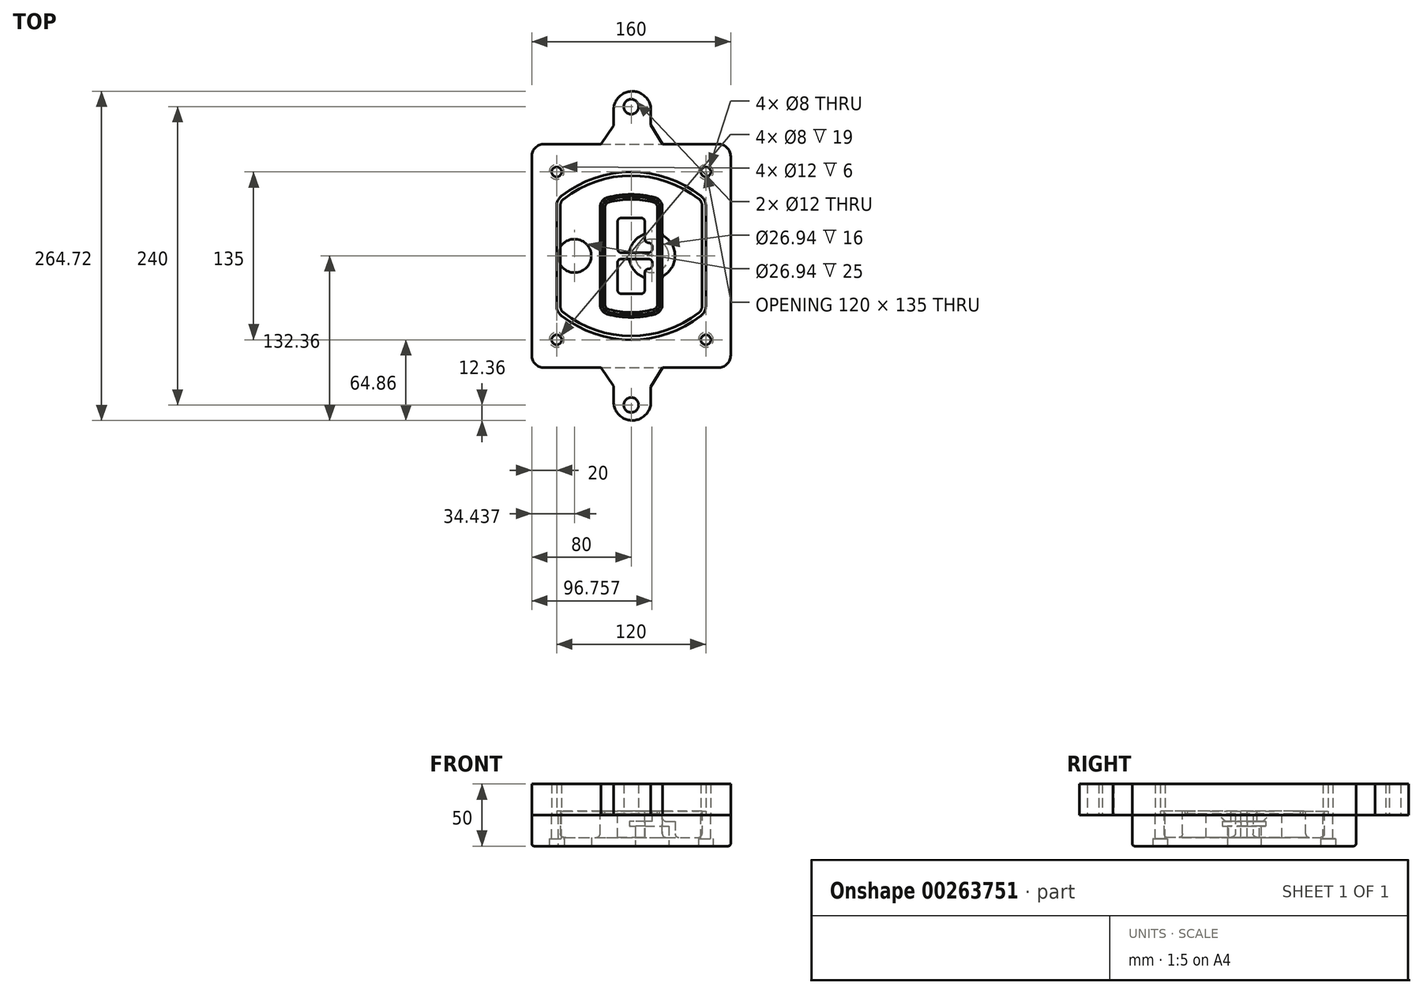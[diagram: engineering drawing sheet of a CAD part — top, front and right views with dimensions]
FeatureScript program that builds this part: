
annotation { "Feature Type Name" : "Feature", "Feature Type Description" : "" }
export const myFeature = defineFeature(function(context is Context, id is Id, definition is map)
    precondition{}
    {
        {
            var Q0;
            Q0=qCreatedBy(makeId("Top.planeOp"),FACE);
            var sketch = newSketch(context, id + "F0", { "sketchPlane" : qUnion([Q0])});
            skPoint(sketch, "E0.rect.middle", {"position": v(0, 0) * mm});
            skLineSegment(sketch, "E1.bottom", {"start": v(-70, -90) * mm, "end": v(70, -90) * mm});
            skLineSegment(sketch, "E1.top", {"start": v(-70, 90) * mm, "end": v(70, 90) * mm});
            skLineSegment(sketch, "E1.left", {"start": v(-80, -80) * mm, "end": v(-80, 80) * mm});
            skLineSegment(sketch, "E1.right", {"start": v(80, -80) * mm, "end": v(80, 80) * mm});
            skLineSegment(sketch, "E2", {"start": v(-80, 90) * mm, "end": v(80, -90) * mm, "construction": true});
            skLineSegment(sketch, "E3", {"start": v(80, 90) * mm, "end": v(-80, -90) * mm, "construction": true});
            skCircle(sketch, "E4", {"center": v(-60, 67.5) * mm, "radius": 4 * mm});
            skCircle(sketch, "E5", {"center": v(60, 67.5) * mm, "radius": 4 * mm});
            skCircle(sketch, "E6", {"center": v(60, -67.5) * mm, "radius": 4 * mm});
            skCircle(sketch, "E7", {"center": v(-60, -67.5) * mm, "radius": 4 * mm});
            skLineSegment(sketch, "E8", {"start": v(-60, 67.5) * mm, "end": v(60, 67.5) * mm, "construction": true});
            skLineSegment(sketch, "E9", {"start": v(60, 67.5) * mm, "end": v(60, -67.5) * mm, "construction": true});
            skLineSegment(sketch, "E10", {"start": v(60, -67.5) * mm, "end": v(-60, -67.5) * mm, "construction": true});
            skLineSegment(sketch, "E11", {"start": v(-60, -67.5) * mm, "end": v(-60, 67.5) * mm, "construction": true});
            skLineSegment(sketch, "E12", {"start": v(-60, 40.3) * mm, "end": v(-60, -40.3) * mm});
            skLineSegment(sketch, "E13", {"start": v(60, 40.3) * mm, "end": v(60, -40.3) * mm});
            skArc(sketch, "E14", {"start": v(56.15, 48.18) * mm, "mid": v(0, 67.5) * mm, "end": v(-56.15, 48.18) * mm});
            skArc(sketch, "E15", {"start": v(-56.15, -48.18) * mm, "mid": v(0, -67.5) * mm, "end": v(56.15, -48.18) * mm});
            skLineSegment(sketch, "E16", {"start": v(-60, 0) * mm, "end": v(60, 0) * mm, "construction": true});
            skPoint(sketch, "E17.visualSharp", {"position": v(-60, -45) * mm});
            skArc(sketch, "E17.filletArc", {"start": v(-60, -40.3) * mm, "mid": v(-58.99, -44.68) * mm, "end": v(-56.15, -48.18) * mm});
            skPoint(sketch, "E18.visualSharp", {"position": v(-60, 45) * mm});
            skArc(sketch, "E18.filletArc", {"start": v(-56.15, 48.18) * mm, "mid": v(-58.99, 44.68) * mm, "end": v(-60, 40.3) * mm});
            skPoint(sketch, "E19.visualSharp", {"position": v(60, 45) * mm});
            skArc(sketch, "E19.filletArc", {"start": v(60, 40.3) * mm, "mid": v(58.99, 44.68) * mm, "end": v(56.15, 48.18) * mm});
            skPoint(sketch, "E20.visualSharp", {"position": v(60, -45) * mm});
            skArc(sketch, "E20.filletArc", {"start": v(56.15, -48.18) * mm, "mid": v(58.99, -44.68) * mm, "end": v(60, -40.3) * mm});
            skPoint(sketch, "E21.visualSharp", {"position": v(-80, 90) * mm});
            skArc(sketch, "E21.filletArc", {"start": v(-70, 90) * mm, "mid": v(-77.07, 87.07) * mm, "end": v(-80, 80) * mm});
            skPoint(sketch, "E22.visualSharp", {"position": v(80, 90) * mm});
            skArc(sketch, "E22.filletArc", {"start": v(80, 80) * mm, "mid": v(77.07, 87.07) * mm, "end": v(70, 90) * mm});
            skPoint(sketch, "E23.visualSharp", {"position": v(80, -90) * mm});
            skArc(sketch, "E23.filletArc", {"start": v(70, -90) * mm, "mid": v(77.07, -87.07) * mm, "end": v(80, -80) * mm});
            skPoint(sketch, "E24.visualSharp", {"position": v(-80, -90) * mm});
            skArc(sketch, "E24.filletArc", {"start": v(-80, -80) * mm, "mid": v(-77.07, -87.07) * mm, "end": v(-70, -90) * mm});
            skArc(sketch, "E25.0", {"start": v(57, 40.3) * mm, "mid": v(56.3, 43.36) * mm, "end": v(54.3, 45.81) * mm});
            skLineSegment(sketch, "E25.1", {"start": v(57, 40.3) * mm, "end": v(57, -40.3) * mm});
            skArc(sketch, "E25.2", {"start": v(54.3, -45.81) * mm, "mid": v(56.3, -43.36) * mm, "end": v(57, -40.3) * mm});
            skArc(sketch, "E25.3", {"start": v(-54.3, -45.81) * mm, "mid": v(0, -64.5) * mm, "end": v(54.3, -45.81) * mm});
            skArc(sketch, "E25.4", {"start": v(-57, -40.3) * mm, "mid": v(-56.3, -43.36) * mm, "end": v(-54.3, -45.81) * mm});
            skArc(sketch, "E25.5", {"start": v(54.3, 45.81) * mm, "mid": v(0, 64.5) * mm, "end": v(-54.3, 45.81) * mm});
            skLineSegment(sketch, "E25.6", {"start": v(-57, 40.3) * mm, "end": v(-57, -40.3) * mm});
            skArc(sketch, "E25.7", {"start": v(-54.3, 45.81) * mm, "mid": v(-56.3, 43.36) * mm, "end": v(-57, 40.3) * mm});
            skArc(sketch, "E26.0", {"start": v(-58.62, 51.33) * mm, "mid": v(-62.58, 46.43) * mm, "end": v(-64, 40.3) * mm});
            skArc(sketch, "E26.1", {"start": v(58.62, 51.33) * mm, "mid": v(0, 71.5) * mm, "end": v(-58.62, 51.33) * mm});
            skArc(sketch, "E26.2", {"start": v(64, 40.3) * mm, "mid": v(62.58, 46.43) * mm, "end": v(58.62, 51.33) * mm});
            skLineSegment(sketch, "E26.3", {"start": v(64, 40.3) * mm, "end": v(64, -40.3) * mm});
            skArc(sketch, "E26.4", {"start": v(58.62, -51.33) * mm, "mid": v(62.58, -46.43) * mm, "end": v(64, -40.3) * mm});
            skLineSegment(sketch, "E26.5", {"start": v(-64, 40.3) * mm, "end": v(-64, -40.3) * mm});
            skArc(sketch, "E26.6", {"start": v(-58.62, -51.33) * mm, "mid": v(0, -71.5) * mm, "end": v(58.62, -51.33) * mm});
            skArc(sketch, "E26.7", {"start": v(-64, -40.3) * mm, "mid": v(-62.58, -46.43) * mm, "end": v(-58.62, -51.33) * mm});
            skSolve(sketch);
        }
        {
            var Q0;
            Q0=makeQuery(id+"F0.imprint","IMPRINT",FACE,{"disambiguationData":[TD([[makeQuery(id+"F0.imprint","IMPRINT",EDGE,{"derivedFrom":sQuery(id+"F0.wireOp",EDGE,"E1.bottom")}),1.0]])]});
            var Q1;
            Q1=makeQuery(id+"F0.imprint","IMPRINT",FACE,{"disambiguationData":[TD([[makeQuery(id+"F0.imprint","IMPRINT",EDGE,{"derivedFrom":sQuery(id+"F0.wireOp",EDGE,"E12")}),1.0]])]});
            var Q2;
            Q2=makeQuery(id+"F0.imprint","IMPRINT",FACE,{"disambiguationData":[TD([[makeQuery(id+"F0.imprint","IMPRINT",EDGE,{"derivedFrom":sQuery(id+"F0.wireOp",EDGE,"E25.0")}),1.0]])]});
            var Q3;
            Q3=makeQuery(id+"F0.imprint","IMPRINT",FACE,{"disambiguationData":[TD([[makeQuery(id+"F0.imprint","IMPRINT",EDGE,{"derivedFrom":sQuery(id+"F0.wireOp",EDGE,"E12")}),-1.0]])]});
            extrude(context, id + "F1", {"entities" : qUnion([Q0, Q1, Q2, Q3]), "oppositeDirection" : true, "depth" : 25 * mm});
        }
        {
            var Q0;
            Q0=makeQuery(id+"F0.imprint","IMPRINT",FACE,{"disambiguationData":[TD([[makeQuery(id+"F0.imprint","IMPRINT",EDGE,{"derivedFrom":sQuery(id+"F0.wireOp",EDGE,"E12")}),1.0]])]});
            extrude(context, id + "F2", {"entities" : qUnion([Q0]), "operationType" : NewBodyOperationType.ADD, "depth" : 3 * mm});
        }
        {
            var Q0;
            Q0=makeQuery(id+"F0.imprint","IMPRINT",FACE,{"disambiguationData":[TD([[makeQuery(id+"F0.imprint","IMPRINT",EDGE,{"derivedFrom":sQuery(id+"F0.wireOp",EDGE,"E25.0")}),1.0]])]});
            extrude(context, id + "F3", {"entities" : qUnion([Q0]), "operationType" : NewBodyOperationType.REMOVE, "oppositeDirection" : true, "depth" : 18 * mm});
        }
        {
            var Q0;
            Q0=makeQuery(id+"F2.opExtrude","CAP_FACE",FACE,{"disambiguationData":[OSD([sQuery(id+"F0.wireOp",EDGE,"E12"),sQuery(id+"F0.wireOp",EDGE,"E13"),sQuery(id+"F0.wireOp",EDGE,"E14"),sQuery(id+"F0.wireOp",EDGE,"E15"),sQuery(id+"F0.wireOp",EDGE,"E17.filletArc"),sQuery(id+"F0.wireOp",EDGE,"E18.filletArc"),sQuery(id+"F0.wireOp",EDGE,"E19.filletArc"),sQuery(id+"F0.wireOp",EDGE,"E20.filletArc"),sQuery(id+"F0.wireOp",EDGE,"E25.0"),sQuery(id+"F0.wireOp",EDGE,"E25.1"),sQuery(id+"F0.wireOp",EDGE,"E25.2"),sQuery(id+"F0.wireOp",EDGE,"E25.3"),sQuery(id+"F0.wireOp",EDGE,"E25.4"),sQuery(id+"F0.wireOp",EDGE,"E25.5"),sQuery(id+"F0.wireOp",EDGE,"E25.6"),sQuery(id+"F0.wireOp",EDGE,"E25.7")])],"isStart":false});
            var sketch = newSketch(context, id + "F4", { "sketchPlane" : qUnion([Q0])});
            skArc(sketch, "E27.0", {"start": v(-19.08, -46.97) * mm, "mid": v(0, -49.5) * mm, "end": v(19.08, -46.97) * mm});
            skArc(sketch, "E28.0", {"start": v(19.08, 46.97) * mm, "mid": v(0, 49.5) * mm, "end": v(-19.08, 46.97) * mm});
            skLineSegment(sketch, "E29", {"start": v(-25, 39.25) * mm, "end": v(-25, -39.25) * mm});
            skLineSegment(sketch, "E30", {"start": v(25, 39.25) * mm, "end": v(25, -39.25) * mm});
            skLineSegment(sketch, "E31", {"start": v(-25, 45.1) * mm, "end": v(25, 45.1) * mm, "construction": true});
            skLineSegment(sketch, "E32", {"start": v(-25, -45.1) * mm, "end": v(25, -45.1) * mm, "construction": true});
            skPoint(sketch, "E33.visualSharp", {"position": v(-25, 45.1) * mm});
            skArc(sketch, "E33.filletArc", {"start": v(-19.08, 46.97) * mm, "mid": v(-23.35, 44.11) * mm, "end": v(-25, 39.25) * mm});
            skPoint(sketch, "E34.visualSharp", {"position": v(25, 45.1) * mm});
            skArc(sketch, "E34.filletArc", {"start": v(25, 39.25) * mm, "mid": v(23.35, 44.11) * mm, "end": v(19.08, 46.97) * mm});
            skPoint(sketch, "E35.visualSharp", {"position": v(25, -45.1) * mm});
            skArc(sketch, "E35.filletArc", {"start": v(19.08, -46.97) * mm, "mid": v(23.35, -44.11) * mm, "end": v(25, -39.25) * mm});
            skPoint(sketch, "E36.visualSharp", {"position": v(-25, -45.1) * mm});
            skArc(sketch, "E36.filletArc", {"start": v(-25, -39.25) * mm, "mid": v(-23.35, -44.11) * mm, "end": v(-19.08, -46.97) * mm});
            skArc(sketch, "E37.0", {"start": v(54.3, 45.81) * mm, "mid": v(0, 64.5) * mm, "end": v(-54.3, 45.81) * mm});
            skArc(sketch, "E37.1", {"start": v(-54.3, 45.81) * mm, "mid": v(-56.3, 43.36) * mm, "end": v(-57, 40.3) * mm});
            skLineSegment(sketch, "E37.2", {"start": v(-57, 40.3) * mm, "end": v(-57, -40.3) * mm});
            skArc(sketch, "E37.3", {"start": v(-57, -40.3) * mm, "mid": v(-56.3, -43.36) * mm, "end": v(-54.3, -45.81) * mm});
            skArc(sketch, "E37.4", {"start": v(-54.3, -45.81) * mm, "mid": v(0, -64.5) * mm, "end": v(54.3, -45.81) * mm});
            skArc(sketch, "E37.5", {"start": v(54.3, -45.81) * mm, "mid": v(56.3, -43.36) * mm, "end": v(57, -40.3) * mm});
            skLineSegment(sketch, "E37.6", {"start": v(57, 40.3) * mm, "end": v(57, -40.3) * mm});
            skArc(sketch, "E37.7", {"start": v(57, 40.3) * mm, "mid": v(56.3, 43.36) * mm, "end": v(54.3, 45.81) * mm});
            skLineSegment(sketch, "E38.0", {"start": v(23, 39.25) * mm, "end": v(23, -39.25) * mm});
            skArc(sketch, "E38.1", {"start": v(18.56, -45.04) * mm, "mid": v(21.76, -42.9) * mm, "end": v(23, -39.25) * mm});
            skArc(sketch, "E38.2", {"start": v(-18.56, -45.04) * mm, "mid": v(0, -47.5) * mm, "end": v(18.56, -45.04) * mm});
            skArc(sketch, "E38.3", {"start": v(-23, -39.25) * mm, "mid": v(-21.76, -42.9) * mm, "end": v(-18.56, -45.04) * mm});
            skLineSegment(sketch, "E38.4", {"start": v(-23, 39.25) * mm, "end": v(-23, -39.25) * mm});
            skArc(sketch, "E38.5", {"start": v(23, 39.25) * mm, "mid": v(21.76, 42.9) * mm, "end": v(18.56, 45.04) * mm});
            skArc(sketch, "E38.6", {"start": v(-18.56, 45.04) * mm, "mid": v(-21.76, 42.9) * mm, "end": v(-23, 39.25) * mm});
            skArc(sketch, "E38.7", {"start": v(18.56, 45.04) * mm, "mid": v(0, 47.5) * mm, "end": v(-18.56, 45.04) * mm});
            skArc(sketch, "E39.0", {"start": v(21, 39.25) * mm, "mid": v(20.18, 41.68) * mm, "end": v(18.04, 43.1) * mm});
            skLineSegment(sketch, "E39.1", {"start": v(21, 39.25) * mm, "end": v(21, -39.25) * mm});
            skArc(sketch, "E39.2", {"start": v(18.04, -43.1) * mm, "mid": v(20.18, -41.68) * mm, "end": v(21, -39.25) * mm});
            skArc(sketch, "E39.3", {"start": v(-18.04, -43.1) * mm, "mid": v(0, -45.5) * mm, "end": v(18.04, -43.1) * mm});
            skArc(sketch, "E39.4", {"start": v(-21, -39.25) * mm, "mid": v(-20.18, -41.68) * mm, "end": v(-18.04, -43.1) * mm});
            skArc(sketch, "E39.5", {"start": v(18.04, 43.1) * mm, "mid": v(0, 45.5) * mm, "end": v(-18.04, 43.1) * mm});
            skLineSegment(sketch, "E39.6", {"start": v(-21, 39.25) * mm, "end": v(-21, -39.25) * mm});
            skArc(sketch, "E39.7", {"start": v(-18.04, 43.1) * mm, "mid": v(-20.18, 41.68) * mm, "end": v(-21, 39.25) * mm});
            skLineSegment(sketch, "E40", {"start": v(-25, 0) * mm, "end": v(25, 0) * mm, "construction": true});
            skLineSegment(sketch, "E41", {"start": v(-11, 5.5) * mm, "end": v(-11, 27.5) * mm});
            skLineSegment(sketch, "E42", {"start": v(-8, 30.5) * mm, "end": v(8, 30.5) * mm});
            skLineSegment(sketch, "E43", {"start": v(11, 27.5) * mm, "end": v(11, 13.5) * mm});
            skLineSegment(sketch, "E44", {"start": v(14, 10.5) * mm, "end": v(14, 10.5) * mm});
            skLineSegment(sketch, "E45", {"start": v(17, 7.5) * mm, "end": v(17, 5.5) * mm});
            skLineSegment(sketch, "E46", {"start": v(14, 2.5) * mm, "end": v(-8, 2.5) * mm});
            skPoint(sketch, "E47.visualSharp", {"position": v(-11, 30.5) * mm});
            skArc(sketch, "E47.filletArc", {"start": v(-8, 30.5) * mm, "mid": v(-10.12, 29.62) * mm, "end": v(-11, 27.5) * mm});
            skPoint(sketch, "E48.visualSharp", {"position": v(11, 30.5) * mm});
            skArc(sketch, "E48.filletArc", {"start": v(11, 27.5) * mm, "mid": v(10.12, 29.62) * mm, "end": v(8, 30.5) * mm});
            skPoint(sketch, "E49.visualSharp", {"position": v(11, 10.5) * mm});
            skArc(sketch, "E49.filletArc", {"start": v(11, 13.5) * mm, "mid": v(11.88, 11.38) * mm, "end": v(14, 10.5) * mm});
            skPoint(sketch, "E50.visualSharp", {"position": v(17, 10.5) * mm});
            skArc(sketch, "E50.filletArc", {"start": v(17, 7.5) * mm, "mid": v(16.12, 9.62) * mm, "end": v(14, 10.5) * mm});
            skPoint(sketch, "E51.visualSharp", {"position": v(17, 2.5) * mm});
            skArc(sketch, "E51.filletArc", {"start": v(14, 2.5) * mm, "mid": v(16.12, 3.38) * mm, "end": v(17, 5.5) * mm});
            skPoint(sketch, "E52.visualSharp", {"position": v(-11, 2.5) * mm});
            skArc(sketch, "E52.filletArc", {"start": v(-11, 5.5) * mm, "mid": v(-10.12, 3.38) * mm, "end": v(-8, 2.5) * mm});
            skLineSegment(sketch, "E53.0.MirrorCS", {"start": v(14, -2.5) * mm, "end": v(-8, -2.5) * mm});
            skArc(sketch, "E54.0.MirrorCS", {"start": v(-11, -5.5) * mm, "mid": v(-10.12, -3.38) * mm, "end": v(-8, -2.5) * mm});
            skLineSegment(sketch, "E55.0.MirrorCS", {"start": v(-11, -5.5) * mm, "end": v(-11, -27.5) * mm});
            skArc(sketch, "E56.0.MirrorCS", {"start": v(-8, -30.5) * mm, "mid": v(-10.12, -29.62) * mm, "end": v(-11, -27.5) * mm});
            skLineSegment(sketch, "E57.0.MirrorCS", {"start": v(-8, -30.5) * mm, "end": v(8, -30.5) * mm});
            skArc(sketch, "E58.0.MirrorCS", {"start": v(11, -27.5) * mm, "mid": v(10.12, -29.62) * mm, "end": v(8, -30.5) * mm});
            skLineSegment(sketch, "E59.0.MirrorCS", {"start": v(11, -27.5) * mm, "end": v(11, -13.5) * mm});
            skArc(sketch, "E60.0.MirrorCS", {"start": v(11, -13.5) * mm, "mid": v(11.88, -11.38) * mm, "end": v(14, -10.5) * mm});
            skArc(sketch, "E61.0.MirrorCS", {"start": v(17, -7.5) * mm, "mid": v(16.12, -9.62) * mm, "end": v(14, -10.5) * mm});
            skLineSegment(sketch, "E62.0.MirrorCS", {"start": v(17, -7.5) * mm, "end": v(17, -5.5) * mm});
            skArc(sketch, "E63.0.MirrorCS", {"start": v(14, -2.5) * mm, "mid": v(16.12, -3.38) * mm, "end": v(17, -5.5) * mm});
            skSolve(sketch);
        }
        {
            var Q0;
            Q0=makeQuery(id+"F4.imprint","IMPRINT",FACE,{"disambiguationData":[TD([[makeQuery(id+"F4.imprint","IMPRINT",EDGE,{"derivedFrom":sQuery(id+"F4.wireOp",EDGE,"E27.0")}),1.0]])]});
            var Q1;
            Q1=makeQuery(id+"F4.imprint","IMPRINT",FACE,{"disambiguationData":[TD([[makeQuery(id+"F4.imprint","IMPRINT",EDGE,{"derivedFrom":sQuery(id+"F4.wireOp",EDGE,"E38.0")}),-1.0]])]});
            var Q2;
            Q2=makeQuery(id+"F4.imprint","IMPRINT",FACE,{"disambiguationData":[TD([[makeQuery(id+"F4.imprint","IMPRINT",EDGE,{"derivedFrom":sQuery(id+"F4.wireOp",EDGE,"E39.0")}),1.0]])]});
            extrude(context, id + "F5", {"entities" : qUnion([Q0, Q1, Q2]), "operationType" : NewBodyOperationType.ADD, "endBound" : BoundingType.UP_TO_NEXT, "oppositeDirection" : true, "depth" : 25 * mm});
        }
        {
            var Q0;
            Q0=makeQuery(id+"F4.imprint","IMPRINT",FACE,{"disambiguationData":[TD([[makeQuery(id+"F4.imprint","IMPRINT",EDGE,{"derivedFrom":sQuery(id+"F4.wireOp",EDGE,"E38.0")}),-1.0]])]});
            extrude(context, id + "F6", {"entities" : qUnion([Q0]), "operationType" : NewBodyOperationType.REMOVE, "oppositeDirection" : true, "depth" : 2 * mm});
        }
        {
            var Q0;
            Q0=makeQuery(id+"F1.opExtrude","CAP_FACE",FACE,{"disambiguationData":[OSD([sQuery(id+"F0.wireOp",EDGE,"E1.bottom"),sQuery(id+"F0.wireOp",EDGE,"E1.top"),sQuery(id+"F0.wireOp",EDGE,"E1.left"),sQuery(id+"F0.wireOp",EDGE,"E1.right"),sQuery(id+"F0.wireOp",EDGE,"E4"),sQuery(id+"F0.wireOp",EDGE,"E5"),sQuery(id+"F0.wireOp",EDGE,"E6"),sQuery(id+"F0.wireOp",EDGE,"E7"),sQuery(id+"F0.wireOp",EDGE,"E21.filletArc"),sQuery(id+"F0.wireOp",EDGE,"E22.filletArc"),sQuery(id+"F0.wireOp",EDGE,"E23.filletArc"),sQuery(id+"F0.wireOp",EDGE,"E24.filletArc")])],"isStart":false});
            var sketch = newSketch(context, id + "F7", { "sketchPlane" : qUnion([Q0])});
            skCircle(sketch, "E64", {"center": v(16.76, 0) * mm, "radius": 13.47 * mm});
            skCircle(sketch, "E65", {"center": v(-45.56, 0) * mm, "radius": 13.47 * mm});
            skLineSegment(sketch, "E66", {"start": v(80, 0) * mm, "end": v(-80, 0) * mm});
            skCircle(sketch, "E67", {"center": v(16.76, 0) * mm, "radius": 18.47 * mm});
            skCircle(sketch, "E68", {"center": v(60, -67.5) * mm, "radius": 6 * mm});
            skCircle(sketch, "E69", {"center": v(-60, -67.5) * mm, "radius": 6 * mm});
            skCircle(sketch, "E70", {"center": v(-60, 67.5) * mm, "radius": 6 * mm});
            skCircle(sketch, "E71", {"center": v(60, 67.5) * mm, "radius": 6 * mm});
            skSolve(sketch);
        }
        {
            var Q0;
            {var subQ1=sQuery(id+"F7.wireOp",EDGE,"E66");var subQ4=sQuery(id+"F7.wireOp",EDGE,"E64");var subQ6=makeQuery(id+"F7.imprint","INTERSECT",VERTEX,{"disambiguationData":[OD(0.0)],"derivedFrom":[subQ4,subQ1]});Q0=makeQuery(id+"F7.imprint","IMPRINT",FACE,{"disambiguationData":[TD([[makeQuery(id+"F7.imprint","IMPRINT",EDGE,{"disambiguationData":[TD([[subQ6,-1.0]])],"derivedFrom":subQ4}),-1.0]])]});}
            var Q1;
            {var subQ0=sQuery(id+"F7.wireOp",EDGE,"E66");var subQ1=sQuery(id+"F7.wireOp",EDGE,"E64");var subQ3=makeQuery(id+"F7.imprint","INTERSECT",VERTEX,{"disambiguationData":[OD(0.0)],"derivedFrom":[subQ1,subQ0]});Q1=makeQuery(id+"F7.imprint","IMPRINT",FACE,{"disambiguationData":[TD([[makeQuery(id+"F7.imprint","IMPRINT",EDGE,{"disambiguationData":[TD([[subQ3,-1.0]])],"derivedFrom":subQ1}),1.0]])]});}
            var Q2;
            {var subQ0=sQuery(id+"F7.wireOp",EDGE,"E66");var subQ1=sQuery(id+"F7.wireOp",EDGE,"E64");var subQ3=makeQuery(id+"F7.imprint","INTERSECT",VERTEX,{"disambiguationData":[OD(0.0)],"derivedFrom":[subQ1,subQ0]});Q2=makeQuery(id+"F7.imprint","IMPRINT",FACE,{"disambiguationData":[TD([[makeQuery(id+"F7.imprint","IMPRINT",EDGE,{"disambiguationData":[TD([[subQ3,1.0]])],"derivedFrom":subQ1}),1.0]])]});}
            var Q3;
            {var subQ1=sQuery(id+"F7.wireOp",EDGE,"E66");var subQ4=sQuery(id+"F7.wireOp",EDGE,"E64");var subQ6=makeQuery(id+"F7.imprint","INTERSECT",VERTEX,{"disambiguationData":[OD(0.0)],"derivedFrom":[subQ4,subQ1]});Q3=makeQuery(id+"F7.imprint","IMPRINT",FACE,{"disambiguationData":[TD([[makeQuery(id+"F7.imprint","IMPRINT",EDGE,{"disambiguationData":[TD([[subQ6,1.0]])],"derivedFrom":subQ4}),-1.0]])]});}
            extrude(context, id + "F8", {"entities" : qUnion([Q0, Q1, Q2, Q3]), "operationType" : NewBodyOperationType.ADD, "oppositeDirection" : true, "depth" : 20 * mm});
        }
        {
            var Q0;
            {var subQ0=sQuery(id+"F7.wireOp",EDGE,"E66");var subQ1=sQuery(id+"F7.wireOp",EDGE,"E64");var subQ3=makeQuery(id+"F7.imprint","INTERSECT",VERTEX,{"disambiguationData":[OD(0.0)],"derivedFrom":[subQ1,subQ0]});Q0=makeQuery(id+"F7.imprint","IMPRINT",FACE,{"disambiguationData":[TD([[makeQuery(id+"F7.imprint","IMPRINT",EDGE,{"disambiguationData":[TD([[subQ3,-1.0]])],"derivedFrom":subQ1}),1.0]])]});}
            var Q1;
            {var subQ0=sQuery(id+"F7.wireOp",EDGE,"E66");var subQ1=sQuery(id+"F7.wireOp",EDGE,"E64");var subQ3=makeQuery(id+"F7.imprint","INTERSECT",VERTEX,{"disambiguationData":[OD(0.0)],"derivedFrom":[subQ1,subQ0]});Q1=makeQuery(id+"F7.imprint","IMPRINT",FACE,{"disambiguationData":[TD([[makeQuery(id+"F7.imprint","IMPRINT",EDGE,{"disambiguationData":[TD([[subQ3,1.0]])],"derivedFrom":subQ1}),1.0]])]});}
            extrude(context, id + "F9", {"entities" : qUnion([Q0, Q1]), "operationType" : NewBodyOperationType.REMOVE, "oppositeDirection" : true, "depth" : 16 * mm});
        }
        {
            var Q0;
            {var subQ0=sQuery(id+"F7.wireOp",EDGE,"E66");var subQ1=sQuery(id+"F7.wireOp",EDGE,"E65");var subQ3=makeQuery(id+"F7.imprint","INTERSECT",VERTEX,{"disambiguationData":[OD(0.0)],"derivedFrom":[subQ1,subQ0]});Q0=makeQuery(id+"F7.imprint","IMPRINT",FACE,{"disambiguationData":[TD([[makeQuery(id+"F7.imprint","IMPRINT",EDGE,{"disambiguationData":[TD([[subQ3,-1.0]])],"derivedFrom":subQ1}),1.0]])]});}
            var Q1;
            {var subQ0=sQuery(id+"F7.wireOp",EDGE,"E66");var subQ1=sQuery(id+"F7.wireOp",EDGE,"E65");var subQ3=makeQuery(id+"F7.imprint","INTERSECT",VERTEX,{"disambiguationData":[OD(0.0)],"derivedFrom":[subQ1,subQ0]});Q1=makeQuery(id+"F7.imprint","IMPRINT",FACE,{"disambiguationData":[TD([[makeQuery(id+"F7.imprint","IMPRINT",EDGE,{"disambiguationData":[TD([[subQ3,1.0]])],"derivedFrom":subQ1}),1.0]])]});}
            extrude(context, id + "F10", {"entities" : qUnion([Q0, Q1]), "operationType" : NewBodyOperationType.REMOVE, "oppositeDirection" : true, "depth" : 25 * mm});
        }
        {
            var Q0;
            Q0=makeQuery(id+"F7.imprint","IMPRINT",FACE,{"disambiguationData":[TD([[makeQuery(id+"F7.imprint","IMPRINT",EDGE,{"derivedFrom":sQuery(id+"F7.wireOp",EDGE,"E68")}),1.0]])]});
            var Q1;
            Q1=makeQuery(id+"F7.imprint","IMPRINT",FACE,{"disambiguationData":[TD([[makeQuery(id+"F7.imprint","IMPRINT",EDGE,{"derivedFrom":makeQuery(id+"F1.opExtrude","CAP_EDGE",EDGE,{"disambiguationData":[OSD([sQuery(id+"F0.wireOp",EDGE,"E5")])],"isStart":false})}),-1.0]])]});
            var Q2;
            Q2=makeQuery(id+"F7.imprint","IMPRINT",FACE,{"disambiguationData":[TD([[makeQuery(id+"F7.imprint","IMPRINT",EDGE,{"derivedFrom":sQuery(id+"F7.wireOp",EDGE,"E69")}),1.0]])]});
            var Q3;
            Q3=makeQuery(id+"F7.imprint","IMPRINT",FACE,{"disambiguationData":[TD([[makeQuery(id+"F7.imprint","IMPRINT",EDGE,{"derivedFrom":makeQuery(id+"F1.opExtrude","CAP_EDGE",EDGE,{"disambiguationData":[OSD([sQuery(id+"F0.wireOp",EDGE,"E4")])],"isStart":false})}),-1.0]])]});
            var Q4;
            Q4=makeQuery(id+"F7.imprint","IMPRINT",FACE,{"disambiguationData":[TD([[makeQuery(id+"F7.imprint","IMPRINT",EDGE,{"derivedFrom":sQuery(id+"F7.wireOp",EDGE,"E70")}),1.0]])]});
            var Q5;
            Q5=makeQuery(id+"F7.imprint","IMPRINT",FACE,{"disambiguationData":[TD([[makeQuery(id+"F7.imprint","IMPRINT",EDGE,{"derivedFrom":makeQuery(id+"F1.opExtrude","CAP_EDGE",EDGE,{"disambiguationData":[OSD([sQuery(id+"F0.wireOp",EDGE,"E7")])],"isStart":false})}),-1.0]])]});
            var Q6;
            Q6=makeQuery(id+"F7.imprint","IMPRINT",FACE,{"disambiguationData":[TD([[makeQuery(id+"F7.imprint","IMPRINT",EDGE,{"derivedFrom":sQuery(id+"F7.wireOp",EDGE,"E71")}),1.0]])]});
            var Q7;
            Q7=makeQuery(id+"F7.imprint","IMPRINT",FACE,{"disambiguationData":[TD([[makeQuery(id+"F7.imprint","IMPRINT",EDGE,{"derivedFrom":makeQuery(id+"F1.opExtrude","CAP_EDGE",EDGE,{"disambiguationData":[OSD([sQuery(id+"F0.wireOp",EDGE,"E6")])],"isStart":false})}),-1.0]])]});
            extrude(context, id + "F11", {"entities" : qUnion([Q0, Q1, Q2, Q3, Q4, Q5, Q6, Q7]), "operationType" : NewBodyOperationType.REMOVE, "oppositeDirection" : true, "depth" : 6 * mm});
        }
        {
            var Q0;
            Q0=makeQuery(id+"F9.boolean.opBoolean","COPY",FACE,{"derivedFrom":makeQuery(id+"F9.opExtrude","CAP_FACE",FACE,{"disambiguationData":[OSD([sQuery(id+"F7.wireOp",EDGE,"E64")])],"isStart":false})});
            var sketch = newSketch(context, id + "F12", { "sketchPlane" : qUnion([Q0])});
            skArc(sketch, "E72.0", {"start": v(11, 17.55) * mm, "mid": v(2.57, 11.82) * mm, "end": v(-1.54, 2.5) * mm});
            skArc(sketch, "E72.1", {"start": v(-1.54, -2.5) * mm, "mid": v(2.57, -11.82) * mm, "end": v(11, -17.55) * mm});
            skLineSegment(sketch, "E73", {"start": v(-1.54, -2.5) * mm, "end": v(14, -2.5) * mm});
            skLineSegment(sketch, "E74.0", {"start": v(14, 2.5) * mm, "end": v(-1.54, 2.5) * mm});
            skArc(sketch, "E74.1", {"start": v(14, 2.5) * mm, "mid": v(16.12, 3.38) * mm, "end": v(17, 5.5) * mm});
            skLineSegment(sketch, "E74.2", {"start": v(17, 7.5) * mm, "end": v(17, 5.5) * mm});
            skArc(sketch, "E74.3", {"start": v(17, 7.5) * mm, "mid": v(16.12, 9.62) * mm, "end": v(14, 10.5) * mm});
            skArc(sketch, "E74.4", {"start": v(11, 13.5) * mm, "mid": v(11.88, 11.38) * mm, "end": v(14, 10.5) * mm});
            skLineSegment(sketch, "E74.5", {"start": v(11, 17.55) * mm, "end": v(11, 13.5) * mm});
            skLineSegment(sketch, "E74.7", {"start": v(14, -2.5) * mm, "end": v(-1.54, -2.5) * mm});
            skArc(sketch, "E74.8", {"start": v(14, -2.5) * mm, "mid": v(16.12, -3.38) * mm, "end": v(17, -5.5) * mm});
            skLineSegment(sketch, "E74.9", {"start": v(17, -7.5) * mm, "end": v(17, -5.5) * mm});
            skArc(sketch, "E74.10", {"start": v(17, -7.5) * mm, "mid": v(16.12, -9.62) * mm, "end": v(14, -10.5) * mm});
            skArc(sketch, "E74.11", {"start": v(11, -13.5) * mm, "mid": v(11.88, -11.38) * mm, "end": v(14, -10.5) * mm});
            skLineSegment(sketch, "E74.12", {"start": v(11, -17.55) * mm, "end": v(11, -13.5) * mm});
            skPoint(sketch, "E75.orphan", {"position": v(11, -27.5) * mm});
            skPoint(sketch, "E76.orphan", {"position": v(-8, -2.5) * mm});
            skPoint(sketch, "E77.orphan", {"position": v(-8, 2.5) * mm});
            skPoint(sketch, "E78.orphan", {"position": v(11, 27.5) * mm});
            skSolve(sketch);
        }
        {
            var Q0;
            {var subQ7=sQuery(id+"F12.wireOp",EDGE,"E72.0");var subQ14=sQuery(id+"F12.wireOp",EDGE,"E72.1");var subQ16=sQuery(id+"F12.wireOp",EDGE,"E74.1");var subQ18=sQuery(id+"F12.wireOp",EDGE,"E74.8");Q0=qUnion([makeQuery(id+"F12.imprint","IMPRINT",FACE,{"disambiguationData":[TD([[makeQuery(id+"F12.imprint","IMPRINT",EDGE,{"derivedFrom":subQ7}),1.0]])]}),makeQuery(id+"F12.imprint","IMPRINT",FACE,{"disambiguationData":[TD([[makeQuery(id+"F12.imprint","IMPRINT",EDGE,{"derivedFrom":subQ14}),1.0]])]}),makeQuery(id+"F12.imprint","IMPRINT",FACE,{"disambiguationData":[TD([[makeQuery(id+"F12.imprint","IMPRINT",EDGE,{"derivedFrom":subQ16}),1.0]])]}),makeQuery(id+"F12.imprint","IMPRINT",FACE,{"disambiguationData":[TD([[makeQuery(id+"F12.imprint","IMPRINT",EDGE,{"derivedFrom":subQ18}),-1.0]])]})]);}
            var Q1;
            Q1=makeQuery(id+"F5.boolean.opBoolean","SPLIT",FACE,{"disambiguationData":[TD([makeQuery(id+"F5.opExtrude","SWEPT_FACE",FACE,{"disambiguationData":[OSD([sQuery(id+"F4.wireOp",EDGE,"E41")])]})])],"derivedFrom":makeQuery(id+"F3.boolean.opBoolean","COPY",FACE,{"derivedFrom":makeQuery(id+"F3.opExtrude","CAP_FACE",FACE,{"disambiguationData":[OSD([sQuery(id+"F0.wireOp",EDGE,"E25.0"),sQuery(id+"F0.wireOp",EDGE,"E25.1"),sQuery(id+"F0.wireOp",EDGE,"E25.2"),sQuery(id+"F0.wireOp",EDGE,"E25.3"),sQuery(id+"F0.wireOp",EDGE,"E25.4"),sQuery(id+"F0.wireOp",EDGE,"E25.5"),sQuery(id+"F0.wireOp",EDGE,"E25.6"),sQuery(id+"F0.wireOp",EDGE,"E25.7")])],"isStart":false})})});
            extrude(context, id + "F13", {"entities" : qUnion([Q0]), "operationType" : NewBodyOperationType.REMOVE, "endBound" : BoundingType.UP_TO_SURFACE, "endBoundEntityFace" : qUnion([Q1]), "depth" : 25 * mm});
        }
        {
            var Q0;
            Q0=makeQuery(id+"F3.boolean.opBoolean","COPY",EDGE,{"derivedFrom":makeQuery(id+"F3.opExtrude","CAP_EDGE",EDGE,{"disambiguationData":[OSD([sQuery(id+"F0.wireOp",EDGE,"E25.6")])],"isStart":false})});
            var Q1;
            Q1=makeQuery(id+"F8.boolean.opBoolean","INTERSECT",EDGE,{"derivedFrom":[makeQuery(id+"F5.opExtrude","SWEPT_FACE",FACE,{"disambiguationData":[OSD([sQuery(id+"F4.wireOp",EDGE,"E30")])]}),makeQuery(id+"F8.opExtrude","CAP_FACE",FACE,{"disambiguationData":[OSD([sQuery(id+"F7.wireOp",EDGE,"E67")])],"isStart":false})]});
            var Q2;
            Q2=makeQuery(id+"F8.boolean.opBoolean","INTERSECT",EDGE,{"disambiguationData":[OD(1.0)],"derivedFrom":[makeQuery(id+"F5.opExtrude","SWEPT_FACE",FACE,{"disambiguationData":[OSD([sQuery(id+"F4.wireOp",EDGE,"E30")])]}),makeQuery(id+"F8.opExtrude","SWEPT_FACE",FACE,{"disambiguationData":[OSD([sQuery(id+"F7.wireOp",EDGE,"E67")])]})]});
            var Q3;
            {var subQ0=sQuery(id+"F4.wireOp",EDGE,"E30");Q3=makeQuery(id+"F8.boolean.opBoolean","SPLIT",EDGE,{"disambiguationData":[TD([makeQuery(id+"F5.opExtrude","SWEPT_FACE",FACE,{"disambiguationData":[OSD([sQuery(id+"F4.wireOp",EDGE,"E35.filletArc")])]})])],"derivedFrom":makeQuery(id+"F5.opExtrude","CAP_EDGE",EDGE,{"disambiguationData":[OSD([subQ0])],"isStart":false})});}
            var Q4;
            {var subQ0=sQuery(id+"F0.wireOp",EDGE,"E25.7");var subQ1=sQuery(id+"F0.wireOp",EDGE,"E25.1");var subQ2=sQuery(id+"F0.wireOp",EDGE,"E25.6");var subQ3=sQuery(id+"F0.wireOp",EDGE,"E25.5");var subQ4=sQuery(id+"F0.wireOp",EDGE,"E25.4");var subQ5=sQuery(id+"F0.wireOp",EDGE,"E25.0");var subQ6=sQuery(id+"F0.wireOp",EDGE,"E25.2");var subQ7=sQuery(id+"F0.wireOp",EDGE,"E25.3");Q4=makeQuery(id+"F8.boolean.opBoolean","INTERSECT",EDGE,{"derivedFrom":[makeQuery(id+"F5.boolean.opBoolean","SPLIT",FACE,{"disambiguationData":[TD([makeQuery(id+"F2.opExtrude","SWEPT_FACE",FACE,{"disambiguationData":[OSD([subQ5])]})])],"derivedFrom":makeQuery(id+"F3.boolean.opBoolean","COPY",FACE,{"derivedFrom":makeQuery(id+"F3.opExtrude","CAP_FACE",FACE,{"disambiguationData":[OSD([subQ5,subQ1,subQ6,subQ7,subQ4,subQ3,subQ2,subQ0])],"isStart":false})})}),makeQuery(id+"F8.opExtrude","SWEPT_FACE",FACE,{"disambiguationData":[OSD([sQuery(id+"F7.wireOp",EDGE,"E67")])]})]});}
            var Q5;
            Q5=makeQuery(id+"F8.boolean.opBoolean","INTERSECT",EDGE,{"disambiguationData":[OD(0.0)],"derivedFrom":[makeQuery(id+"F5.opExtrude","SWEPT_FACE",FACE,{"disambiguationData":[OSD([sQuery(id+"F4.wireOp",EDGE,"E30")])]}),makeQuery(id+"F8.opExtrude","SWEPT_FACE",FACE,{"disambiguationData":[OSD([sQuery(id+"F7.wireOp",EDGE,"E67")])]})]});
            fillet(context, id + "F14", {"entities" : qUnion([Q0, Q1, Q2, Q3, Q4, Q5]), "radius" : 3 * mm, "tangentPropagation" : true, "allowEdgeOverflow" : false});
        }
        {
            var Q0;
            Q0=makeQuery(id+"F1.opExtrude","CAP_EDGE",EDGE,{"disambiguationData":[OSD([sQuery(id+"F0.wireOp",EDGE,"E1.bottom")])],"isStart":false});
            fillet(context, id + "F15", {"entities" : qUnion([Q0]), "radius" : 2 * mm, "tangentPropagation" : true, "allowEdgeOverflow" : false});
        }
        {
            var Q0;
            {var subQ0=sQuery(id+"F0.wireOp",EDGE,"E22.filletArc");var subQ1=sQuery(id+"F0.wireOp",EDGE,"E7");var subQ2=sQuery(id+"F0.wireOp",EDGE,"E6");var subQ3=sQuery(id+"F0.wireOp",EDGE,"E5");var subQ4=sQuery(id+"F0.wireOp",EDGE,"E4");var subQ5=sQuery(id+"F0.wireOp",EDGE,"E1.bottom");var subQ6=sQuery(id+"F0.wireOp",EDGE,"E21.filletArc");var subQ7=sQuery(id+"F0.wireOp",EDGE,"E1.top");var subQ8=sQuery(id+"F0.wireOp",EDGE,"E1.left");var subQ9=sQuery(id+"F0.wireOp",EDGE,"E1.right");var subQ10=sQuery(id+"F0.wireOp",EDGE,"E23.filletArc");var subQ11=sQuery(id+"F0.wireOp",EDGE,"E24.filletArc");Q0=makeQuery(id+"F2.boolean.opBoolean","SPLIT",FACE,{"disambiguationData":[TD([makeQuery(id+"F1.opExtrude","SWEPT_FACE",FACE,{"disambiguationData":[OSD([subQ5])]})])],"derivedFrom":makeQuery(id+"F1.opExtrude","CAP_FACE",FACE,{"disambiguationData":[OSD([subQ5,subQ7,subQ8,subQ9,subQ4,subQ3,subQ2,subQ1,subQ6,subQ0,subQ10,subQ11])],"isStart":true})});}
            var sketch = newSketch(context, id + "F16", { "sketchPlane" : qUnion([Q0])});
            skLineSegment(sketch, "E79", {"start": v(0, -90) * mm, "end": v(0, -120) * mm});
            skPoint(sketch, "E79.endSnap0", {"position": v(0, -90) * mm});
            skLineSegment(sketch, "E80", {"start": v(-14.14, -104.83) * mm, "end": v(-14.14, -116.83) * mm});
            skLineSegment(sketch, "E81", {"start": v(15.85, -105.36) * mm, "end": v(15.85, -117.36) * mm});
            skArc(sketch, "E82", {"start": v(-14.14, -116.83) * mm, "mid": v(0.58, -132.36) * mm, "end": v(15.85, -117.36) * mm});
            skCircle(sketch, "E83", {"center": v(0, -120) * mm, "radius": 6 * mm});
            skLineSegment(sketch, "E84", {"start": v(-14.14, -104.83) * mm, "end": v(-24.34, -90) * mm});
            skLineSegment(sketch, "E85", {"start": v(15.85, -105.36) * mm, "end": v(25.23, -90) * mm});
            skLineSegment(sketch, "E86", {"start": v(0, 0) * mm, "end": v(-15.48, 0) * mm});
            skLineSegment(sketch, "E87", {"start": v(-15.48, 0) * mm, "end": v(0, 0) * mm});
            skLineSegment(sketch, "E88", {"start": v(19.94, 0) * mm, "end": v(0, 0) * mm});
            skPoint(sketch, "E89.MirrorP", {"position": v(0, 90) * mm});
            skLineSegment(sketch, "E90.MirrorCS", {"start": v(15.85, 105.36) * mm, "end": v(15.85, 117.36) * mm});
            skCircle(sketch, "E91.MirrorC", {"center": v(0, 120) * mm, "radius": 6 * mm});
            skLineSegment(sketch, "E92.MirrorCS", {"start": v(-14.14, 104.83) * mm, "end": v(-14.14, 116.83) * mm});
            skArc(sketch, "E93.MirrorCS", {"start": v(-14.14, 116.83) * mm, "mid": v(0.58, 132.36) * mm, "end": v(15.85, 117.36) * mm});
            skLineSegment(sketch, "E94.MirrorCS", {"start": v(0, 90) * mm, "end": v(0, 120) * mm});
            skLineSegment(sketch, "E95.MirrorCS", {"start": v(-14.14, 104.83) * mm, "end": v(-24.34, 90) * mm});
            skLineSegment(sketch, "E96.MirrorCS", {"start": v(15.85, 105.36) * mm, "end": v(25.23, 90) * mm});
            skSolve(sketch);
        }
        {
            var Q0;
            Q0=makeQuery(id+"F16.imprint","IMPRINT",FACE,{"disambiguationData":[TD([[makeQuery(id+"F16.imprint","IMPRINT",EDGE,{"derivedFrom":sQuery(id+"F16.wireOp",EDGE,"E90.MirrorCS")}),1.0]])]});
            var Q1;
            Q1=makeQuery(id+"F16.imprint","IMPRINT",FACE,{"disambiguationData":[TD([[makeQuery(id+"F16.imprint","IMPRINT",EDGE,{"derivedFrom":sQuery(id+"F16.wireOp",EDGE,"E80")}),1.0]])]});
            var Q2;
            Q2=makeQuery(id+"F16.imprint","IMPRINT",FACE,{"disambiguationData":[TD([[makeQuery(id+"F16.imprint","IMPRINT",EDGE,{"derivedFrom":makeQuery(id+"F1.opExtrude","CAP_EDGE",EDGE,{"disambiguationData":[OSD([sQuery(id+"F0.wireOp",EDGE,"E1.left")])],"isStart":true})}),-1.0]])]});
            extrude(context, id + "F17", {"entities" : qUnion([Q0, Q1, Q2]), "depth" : 25 * mm});
        }
    });
